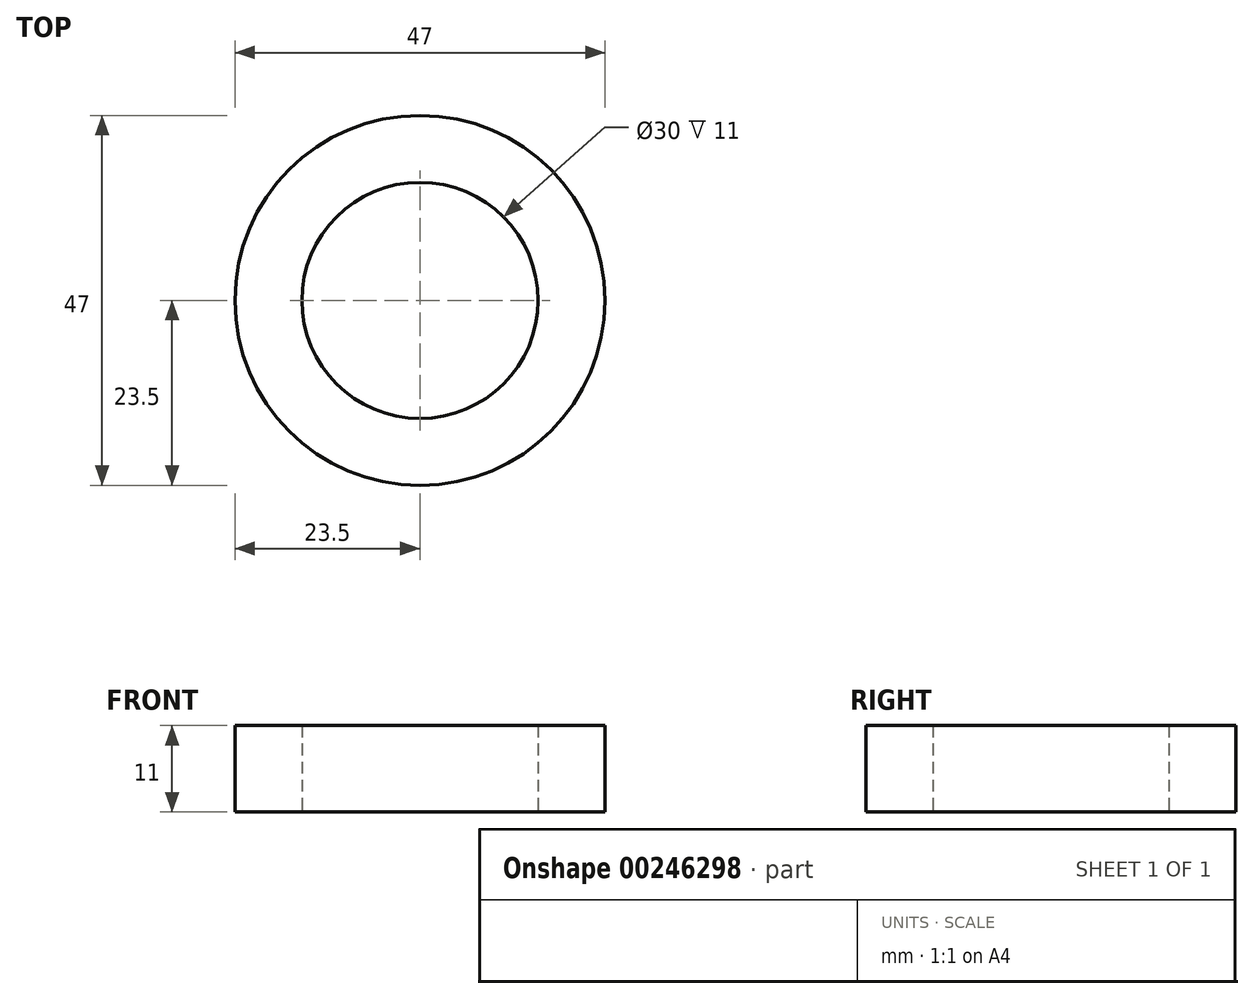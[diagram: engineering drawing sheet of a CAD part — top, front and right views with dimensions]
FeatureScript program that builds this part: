
annotation { "Feature Type Name" : "Feature", "Feature Type Description" : "" }
export const myFeature = defineFeature(function(context is Context, id is Id, definition is map)
    precondition{}
    {
        {
            var Q0;
            Q0=qCreatedBy(makeId("Top.planeOp"),FACE);
            var sketch = newSketch(context, id + "F0", { "sketchPlane" : qUnion([Q0])});
            skCircle(sketch, "E0", {"center": v(0, 0) * mm, "radius": 15 * mm});
            skCircle(sketch, "E1", {"center": v(0, 0) * mm, "radius": 23.5 * mm});
            skSolve(sketch);
        }
        {
            var Q0;
            Q0 = qSketchRegion(id + "F0", true);
            extrude(context, id + "F1", {"entities" : qUnion([Q0]), "depth" : 11 * mm});
        }
    });
